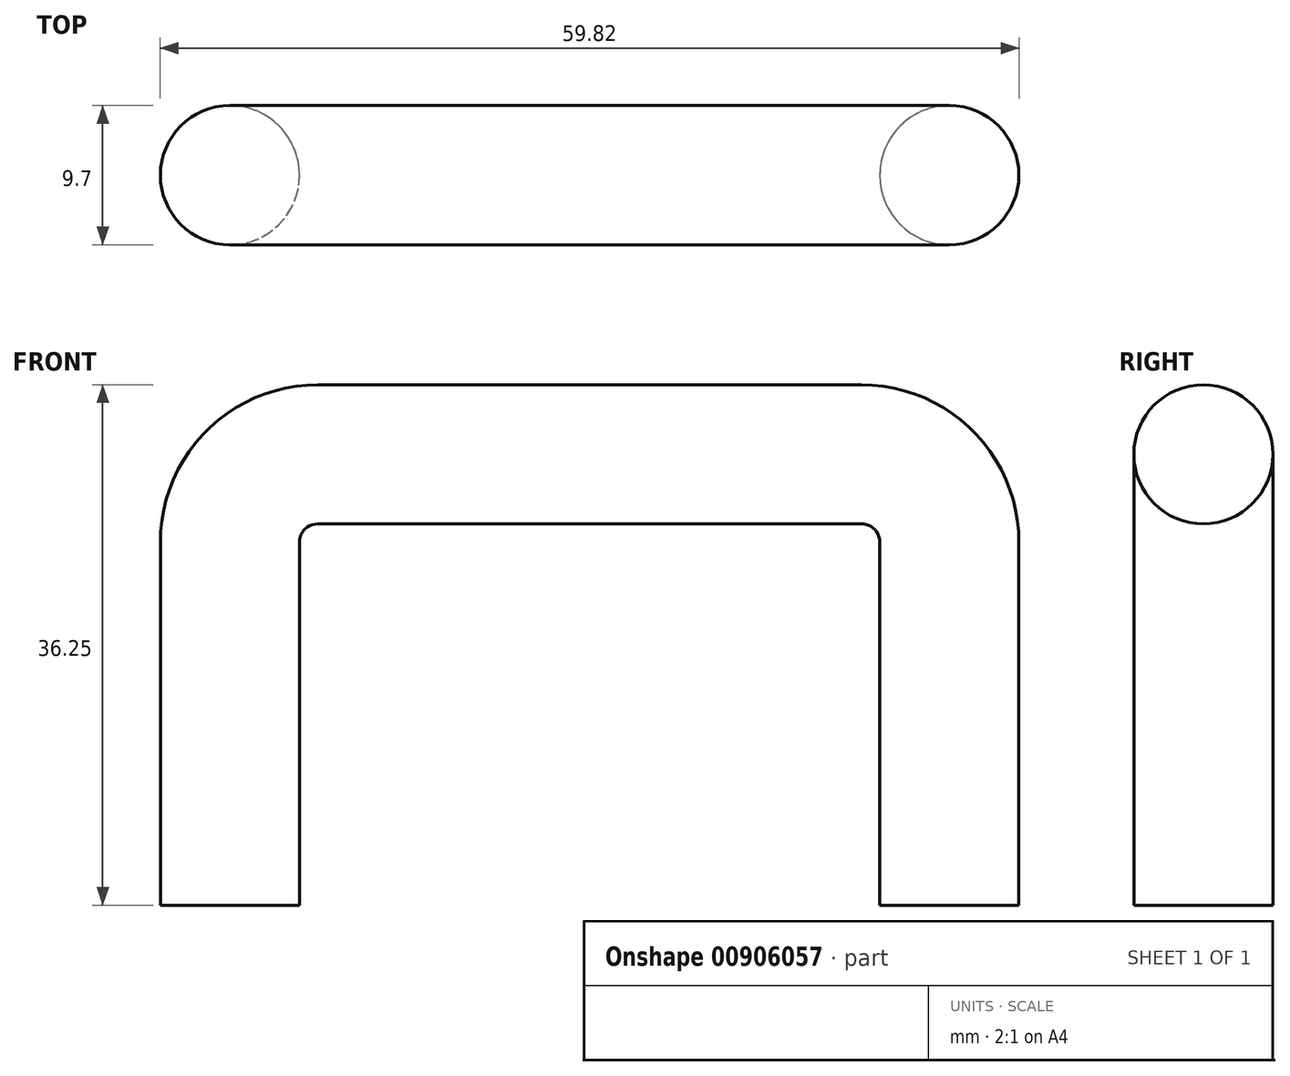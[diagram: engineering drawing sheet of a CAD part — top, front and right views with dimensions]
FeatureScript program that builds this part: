
annotation { "Feature Type Name" : "Feature", "Feature Type Description" : "" }
export const myFeature = defineFeature(function(context is Context, id is Id, definition is map)
    precondition{}
    {
        {
            var Q0;
            Q0=qCreatedBy(makeId("Front.planeOp"),FACE);
            var sketch = newSketch(context, id + "F0", { "sketchPlane" : qUnion([Q0])});
            skLineSegment(sketch, "E0", {"start": v(-27.12, 0) * mm, "end": v(-27.12, 25.3) * mm});
            skLineSegment(sketch, "E1", {"start": v(-20.77, 31.64) * mm, "end": v(17.11, 31.64) * mm});
            skLineSegment(sketch, "E2", {"start": v(23.46, 25.3) * mm, "end": v(23.46, 0) * mm});
            skPoint(sketch, "E3.visualSharp", {"position": v(-27.12, 31.64) * mm});
            skArc(sketch, "E3.filletArc", {"start": v(-20.77, 31.64) * mm, "mid": v(-25.26, 29.78) * mm, "end": v(-27.12, 25.3) * mm});
            skPoint(sketch, "E4.visualSharp", {"position": v(23.46, 31.64) * mm});
            skArc(sketch, "E4.filletArc", {"start": v(23.46, 25.3) * mm, "mid": v(21.6, 29.78) * mm, "end": v(17.11, 31.64) * mm});
            skSolve(sketch);
        }
        {
            var Q0;
            Q0=qCreatedBy(makeId("Top.planeOp"),FACE);
            var sketch = newSketch(context, id + "F1", { "sketchPlane" : qUnion([Q0])});
            skCircle(sketch, "E5", {"center": v(23.23, 0) * mm, "radius": 4.85 * mm});
            skSolve(sketch);
        }
        {
            var Q0;
            Q0=makeQuery(id+"F1.imprint","IMPRINT",FACE,{"disambiguationData":[TD([[makeQuery(id+"F1.imprint","IMPRINT",EDGE,{"derivedFrom":sQuery(id+"F1.wireOp",EDGE,"E5")}),1.0]])]});
            var Q1;
            Q1=sQuery(id+"F0.wireOp",EDGE,"E2");
            var Q2;
            Q2=sQuery(id+"F0.wireOp",EDGE,"E4.filletArc");
            var Q3;
            Q3=sQuery(id+"F0.wireOp",EDGE,"E1");
            var Q4;
            Q4=sQuery(id+"F0.wireOp",EDGE,"E3.filletArc");
            var Q5;
            Q5=sQuery(id+"F0.wireOp",EDGE,"E0");
            sweep(context, id + "F2", {"profiles" : qUnion([Q0]), "path" : qUnion([Q1, Q2, Q3, Q4, Q5])});
        }
    });
